# Revit family: OASIS SH-WX-4838 STD
name_source: partatom
category: Plumbing Fixtures
revit_build: Autodesk Revit 2017 (Build: 20171027_0315(x64)
units: mm (PartAtom-declared; Revit-internal decimal feet)

## family parameters
Always vertical = Yes
Cut with Voids When Loaded = No
OmniClass Number = 23.45.05.14.21.11
OmniClass Title = Bath/Shower Units
Part Type = Normal
Room Calculation Point = No
Round Connector Dimension = Use Diameter
Shared = No
Work Plane-Based = No

## types (7) — shared parameters
BIM Model By = www.epoch-design.com
Color = <By Category>
Grab Bar Finish = <By Category>
Manufacturer = OASIS
Seat Finish = <By Category>
Shower Rod = No
Stainless steel = <By Category>
Type Comments = Shower or Combination Tub & Shower
URL = www.oasisbath.com

## per-type parameters (varying)
| type | Bar_Horz_Back | Bar_Horz_Left | Bar_Horz_Right | Bar_Vert | Model | Seat_Fold |
| Base Model, FH, FHV, 3SM, & 3SF packages | No | No | No | No | SH-WX-4838 /(Base Model,FH,FHV,3SM,3SF) | No |
| BP1 package | Yes | Yes | No | No | SH-WX-4838/BP1(R,L) | No |
| BP2 package | Yes | Yes | No | Yes | SH-WX-4838/BP2(R,L) | No |
| BP5 package | Yes | No | No | No | SH-WX-4838/BP5 | No |
| TL package | Yes | Yes | No | No | SH-WX-4838/TL(RS,LS) | Yes |
| TLV package | Yes | Yes | No | Yes | SH-WX-4838/TLV(RS,LS) | Yes |
| BP3 package | Yes | Yes | Yes | No | SH-WX-4838/BP3 | No |

## geometry (parser evidence)
native form markers: Sweep x10
no freeform markers — native parametric forms only
